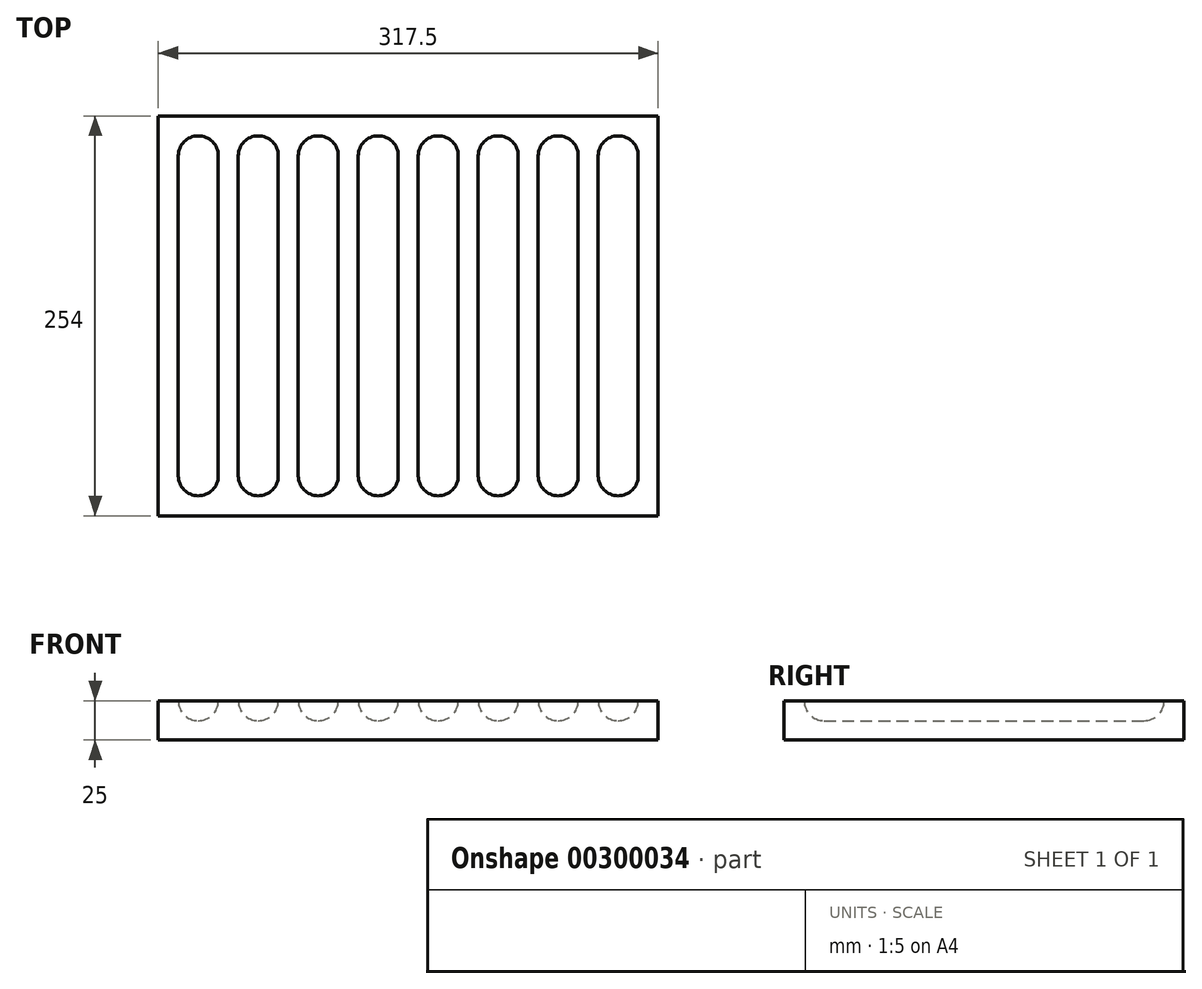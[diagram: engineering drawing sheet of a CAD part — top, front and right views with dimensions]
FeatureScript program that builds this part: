
annotation { "Feature Type Name" : "Feature", "Feature Type Description" : "" }
export const myFeature = defineFeature(function(context is Context, id is Id, definition is map)
    precondition{}
    {
        {
            var Q0;
            Q0=qCreatedBy(makeId("Top.planeOp"),FACE);
            var sketch = newSketch(context, id + "F0", { "sketchPlane" : qUnion([Q0])});
            skLineSegment(sketch, "E0.bottom", {"start": v(-140.22, 133.8) * mm, "end": v(177.28, 133.8) * mm});
            skLineSegment(sketch, "E0.top", {"start": v(-140.22, -120.2) * mm, "end": v(177.28, -120.2) * mm});
            skLineSegment(sketch, "E0.left", {"start": v(-140.22, 133.8) * mm, "end": v(-140.22, -120.2) * mm});
            skLineSegment(sketch, "E0.right", {"start": v(177.28, 133.8) * mm, "end": v(177.28, -120.2) * mm});
            skLineSegment(sketch, "E1.bottom", {"start": v(-127.52, 108.4) * mm, "end": v(-102.12, 108.4) * mm, "construction": true});
            skLineSegment(sketch, "E1.top", {"start": v(-127.52, -94.8) * mm, "end": v(-102.12, -94.8) * mm, "construction": true});
            skLineSegment(sketch, "E1.left", {"start": v(-127.52, 108.4) * mm, "end": v(-127.52, -94.8) * mm});
            skLineSegment(sketch, "E1.right", {"start": v(-102.12, 108.4) * mm, "end": v(-102.12, -94.8) * mm});
            skArc(sketch, "E2", {"start": v(-127.52, 108.4) * mm, "mid": v(-114.82, 121.1) * mm, "end": v(-102.12, 108.4) * mm});
            skArc(sketch, "E3", {"start": v(-102.12, -94.8) * mm, "mid": v(-114.82, -107.5) * mm, "end": v(-127.52, -94.8) * mm});
            skLineSegment(sketch, "E4.1.0.0", {"start": v(-89.42, 108.4) * mm, "end": v(-89.42, -94.8) * mm});
            skArc(sketch, "E4.1.0.1", {"start": v(-89.42, 108.4) * mm, "mid": v(-76.72, 121.1) * mm, "end": v(-64.02, 108.4) * mm});
            skLineSegment(sketch, "E4.1.0.2", {"start": v(-64.02, 108.4) * mm, "end": v(-64.02, -94.8) * mm});
            skArc(sketch, "E4.1.0.3", {"start": v(-64.02, -94.8) * mm, "mid": v(-76.72, -107.5) * mm, "end": v(-89.42, -94.8) * mm});
            skLineSegment(sketch, "E4.1.0.4", {"start": v(-89.42, -94.8) * mm, "end": v(-64.02, -94.8) * mm, "construction": true});
            skLineSegment(sketch, "E4.1.0.5", {"start": v(-89.42, 108.4) * mm, "end": v(-64.02, 108.4) * mm, "construction": true});
            skLineSegment(sketch, "E4.2.0.0", {"start": v(-51.32, 108.4) * mm, "end": v(-51.32, -94.8) * mm});
            skArc(sketch, "E4.2.0.1", {"start": v(-51.32, 108.4) * mm, "mid": v(-38.62, 121.1) * mm, "end": v(-25.92, 108.4) * mm});
            skLineSegment(sketch, "E4.2.0.2", {"start": v(-25.92, 108.4) * mm, "end": v(-25.92, -94.8) * mm});
            skArc(sketch, "E4.2.0.3", {"start": v(-25.92, -94.8) * mm, "mid": v(-38.62, -107.5) * mm, "end": v(-51.32, -94.8) * mm});
            skLineSegment(sketch, "E4.2.0.4", {"start": v(-51.32, -94.8) * mm, "end": v(-25.92, -94.8) * mm, "construction": true});
            skLineSegment(sketch, "E4.2.0.5", {"start": v(-51.32, 108.4) * mm, "end": v(-25.92, 108.4) * mm, "construction": true});
            skLineSegment(sketch, "E4.3.0.0", {"start": v(-13.22, 108.4) * mm, "end": v(-13.22, -94.8) * mm});
            skArc(sketch, "E4.3.0.1", {"start": v(-13.22, 108.4) * mm, "mid": v(-0.52, 121.1) * mm, "end": v(12.18, 108.4) * mm});
            skLineSegment(sketch, "E4.3.0.2", {"start": v(12.18, 108.4) * mm, "end": v(12.18, -94.8) * mm});
            skArc(sketch, "E4.3.0.3", {"start": v(12.18, -94.8) * mm, "mid": v(-0.52, -107.5) * mm, "end": v(-13.22, -94.8) * mm});
            skLineSegment(sketch, "E4.3.0.4", {"start": v(-13.22, -94.8) * mm, "end": v(12.18, -94.8) * mm, "construction": true});
            skLineSegment(sketch, "E4.3.0.5", {"start": v(-13.22, 108.4) * mm, "end": v(12.18, 108.4) * mm, "construction": true});
            skLineSegment(sketch, "E4.4.0.0", {"start": v(24.88, 108.4) * mm, "end": v(24.88, -94.8) * mm});
            skArc(sketch, "E4.4.0.1", {"start": v(24.88, 108.4) * mm, "mid": v(37.58, 121.1) * mm, "end": v(50.28, 108.4) * mm});
            skLineSegment(sketch, "E4.4.0.2", {"start": v(50.28, 108.4) * mm, "end": v(50.28, -94.8) * mm});
            skArc(sketch, "E4.4.0.3", {"start": v(50.28, -94.8) * mm, "mid": v(37.58, -107.5) * mm, "end": v(24.88, -94.8) * mm});
            skLineSegment(sketch, "E4.4.0.4", {"start": v(24.88, -94.8) * mm, "end": v(50.28, -94.8) * mm, "construction": true});
            skLineSegment(sketch, "E4.4.0.5", {"start": v(24.88, 108.4) * mm, "end": v(50.28, 108.4) * mm, "construction": true});
            skLineSegment(sketch, "E4.5.0.0", {"start": v(62.98, 108.4) * mm, "end": v(62.98, -94.8) * mm});
            skArc(sketch, "E4.5.0.1", {"start": v(62.98, 108.4) * mm, "mid": v(75.68, 121.1) * mm, "end": v(88.38, 108.4) * mm});
            skLineSegment(sketch, "E4.5.0.2", {"start": v(88.38, 108.4) * mm, "end": v(88.38, -94.8) * mm});
            skArc(sketch, "E4.5.0.3", {"start": v(88.38, -94.8) * mm, "mid": v(75.68, -107.5) * mm, "end": v(62.98, -94.8) * mm});
            skLineSegment(sketch, "E4.5.0.4", {"start": v(62.98, -94.8) * mm, "end": v(88.38, -94.8) * mm, "construction": true});
            skLineSegment(sketch, "E4.5.0.5", {"start": v(62.98, 108.4) * mm, "end": v(88.38, 108.4) * mm, "construction": true});
            skLineSegment(sketch, "E4.6.0.0", {"start": v(101.08, 108.4) * mm, "end": v(101.08, -94.8) * mm});
            skArc(sketch, "E4.6.0.1", {"start": v(101.08, 108.4) * mm, "mid": v(113.78, 121.1) * mm, "end": v(126.48, 108.4) * mm});
            skLineSegment(sketch, "E4.6.0.2", {"start": v(126.48, 108.4) * mm, "end": v(126.48, -94.8) * mm});
            skArc(sketch, "E4.6.0.3", {"start": v(126.48, -94.8) * mm, "mid": v(113.78, -107.5) * mm, "end": v(101.08, -94.8) * mm});
            skLineSegment(sketch, "E4.6.0.4", {"start": v(101.08, -94.8) * mm, "end": v(126.48, -94.8) * mm, "construction": true});
            skLineSegment(sketch, "E4.6.0.5", {"start": v(101.08, 108.4) * mm, "end": v(126.48, 108.4) * mm, "construction": true});
            skLineSegment(sketch, "E4.7.0.0", {"start": v(139.18, 108.4) * mm, "end": v(139.18, -94.8) * mm});
            skArc(sketch, "E4.7.0.1", {"start": v(139.18, 108.4) * mm, "mid": v(151.88, 121.1) * mm, "end": v(164.58, 108.4) * mm});
            skLineSegment(sketch, "E4.7.0.2", {"start": v(164.58, 108.4) * mm, "end": v(164.58, -94.8) * mm});
            skArc(sketch, "E4.7.0.3", {"start": v(164.58, -94.8) * mm, "mid": v(151.88, -107.5) * mm, "end": v(139.18, -94.8) * mm});
            skLineSegment(sketch, "E4.7.0.4", {"start": v(139.18, -94.8) * mm, "end": v(164.58, -94.8) * mm, "construction": true});
            skLineSegment(sketch, "E4.7.0.5", {"start": v(139.18, 108.4) * mm, "end": v(164.58, 108.4) * mm, "construction": true});
            skLineSegment(sketch, "E4.direction1", {"start": v(-127.52, -94.8) * mm, "end": v(-89.42, -94.8) * mm, "construction": true});
            skSolve(sketch);
        }
        {
            var Q0;
            Q0=makeQuery(id+"F0.imprint","IMPRINT",FACE,{"disambiguationData":[TD([[makeQuery(id+"F0.imprint","IMPRINT",EDGE,{"derivedFrom":sQuery(id+"F0.wireOp",EDGE,"E0.bottom")}),-1.0]])]});
            var Q1;
            Q1=makeQuery(id+"F0.imprint","IMPRINT",FACE,{"disambiguationData":[TD([[makeQuery(id+"F0.imprint","IMPRINT",EDGE,{"derivedFrom":sQuery(id+"F0.wireOp",EDGE,"E1.left")}),1.0]])]});
            var Q2;
            Q2=makeQuery(id+"F0.imprint","IMPRINT",FACE,{"disambiguationData":[TD([[makeQuery(id+"F0.imprint","IMPRINT",EDGE,{"derivedFrom":sQuery(id+"F0.wireOp",EDGE,"E4.1.0.0")}),1.0]])]});
            var Q3;
            Q3=makeQuery(id+"F0.imprint","IMPRINT",FACE,{"disambiguationData":[TD([[makeQuery(id+"F0.imprint","IMPRINT",EDGE,{"derivedFrom":sQuery(id+"F0.wireOp",EDGE,"E4.2.0.0")}),1.0]])]});
            var Q4;
            Q4=makeQuery(id+"F0.imprint","IMPRINT",FACE,{"disambiguationData":[TD([[makeQuery(id+"F0.imprint","IMPRINT",EDGE,{"derivedFrom":sQuery(id+"F0.wireOp",EDGE,"E4.3.0.0")}),1.0]])]});
            var Q5;
            Q5=makeQuery(id+"F0.imprint","IMPRINT",FACE,{"disambiguationData":[TD([[makeQuery(id+"F0.imprint","IMPRINT",EDGE,{"derivedFrom":sQuery(id+"F0.wireOp",EDGE,"E4.4.0.0")}),1.0]])]});
            var Q6;
            Q6=makeQuery(id+"F0.imprint","IMPRINT",FACE,{"disambiguationData":[TD([[makeQuery(id+"F0.imprint","IMPRINT",EDGE,{"derivedFrom":sQuery(id+"F0.wireOp",EDGE,"E4.5.0.0")}),1.0]])]});
            var Q7;
            Q7=makeQuery(id+"F0.imprint","IMPRINT",FACE,{"disambiguationData":[TD([[makeQuery(id+"F0.imprint","IMPRINT",EDGE,{"derivedFrom":sQuery(id+"F0.wireOp",EDGE,"E4.6.0.0")}),1.0]])]});
            var Q8;
            Q8=makeQuery(id+"F0.imprint","IMPRINT",FACE,{"disambiguationData":[TD([[makeQuery(id+"F0.imprint","IMPRINT",EDGE,{"derivedFrom":sQuery(id+"F0.wireOp",EDGE,"E4.7.0.0")}),1.0]])]});
            extrude(context, id + "F1", {"entities" : qUnion([Q0, Q1, Q2, Q3, Q4, Q5, Q6, Q7, Q8]), "oppositeDirection" : true, "depth" : 25 * mm});
        }
        {
            var Q0;
            Q0=makeQuery(id+"F0.imprint","IMPRINT",FACE,{"disambiguationData":[TD([[makeQuery(id+"F0.imprint","IMPRINT",EDGE,{"derivedFrom":sQuery(id+"F0.wireOp",EDGE,"E1.left")}),1.0]])]});
            var Q1;
            Q1=makeQuery(id+"F0.imprint","IMPRINT",FACE,{"disambiguationData":[TD([[makeQuery(id+"F0.imprint","IMPRINT",EDGE,{"derivedFrom":sQuery(id+"F0.wireOp",EDGE,"E4.1.0.0")}),1.0]])]});
            var Q2;
            Q2=makeQuery(id+"F0.imprint","IMPRINT",FACE,{"disambiguationData":[TD([[makeQuery(id+"F0.imprint","IMPRINT",EDGE,{"derivedFrom":sQuery(id+"F0.wireOp",EDGE,"E4.2.0.0")}),1.0]])]});
            var Q3;
            Q3=makeQuery(id+"F0.imprint","IMPRINT",FACE,{"disambiguationData":[TD([[makeQuery(id+"F0.imprint","IMPRINT",EDGE,{"derivedFrom":sQuery(id+"F0.wireOp",EDGE,"E4.3.0.0")}),1.0]])]});
            var Q4;
            Q4=makeQuery(id+"F0.imprint","IMPRINT",FACE,{"disambiguationData":[TD([[makeQuery(id+"F0.imprint","IMPRINT",EDGE,{"derivedFrom":sQuery(id+"F0.wireOp",EDGE,"E4.4.0.0")}),1.0]])]});
            var Q5;
            Q5=makeQuery(id+"F0.imprint","IMPRINT",FACE,{"disambiguationData":[TD([[makeQuery(id+"F0.imprint","IMPRINT",EDGE,{"derivedFrom":sQuery(id+"F0.wireOp",EDGE,"E4.5.0.0")}),1.0]])]});
            var Q6;
            Q6=makeQuery(id+"F0.imprint","IMPRINT",FACE,{"disambiguationData":[TD([[makeQuery(id+"F0.imprint","IMPRINT",EDGE,{"derivedFrom":sQuery(id+"F0.wireOp",EDGE,"E4.6.0.0")}),1.0]])]});
            var Q7;
            Q7=makeQuery(id+"F0.imprint","IMPRINT",FACE,{"disambiguationData":[TD([[makeQuery(id+"F0.imprint","IMPRINT",EDGE,{"derivedFrom":sQuery(id+"F0.wireOp",EDGE,"E4.7.0.0")}),1.0]])]});
            extrude(context, id + "F2", {"entities" : qUnion([Q0, Q1, Q2, Q3, Q4, Q5, Q6, Q7]), "operationType" : NewBodyOperationType.REMOVE, "oppositeDirection" : true, "depth" : 12.7 * mm});
        }
        {
            var Q0;
            Q0=makeQuery(id+"F2.boolean.opBoolean","COPY",EDGE,{"derivedFrom":makeQuery(id+"F2.opExtrude","CAP_EDGE",EDGE,{"disambiguationData":[OSD([sQuery(id+"F0.wireOp",EDGE,"E1.left")])],"isStart":false})});
            var Q1;
            Q1=makeQuery(id+"F2.boolean.opBoolean","COPY",EDGE,{"derivedFrom":makeQuery(id+"F2.opExtrude","CAP_EDGE",EDGE,{"disambiguationData":[OSD([sQuery(id+"F0.wireOp",EDGE,"E4.1.0.0")])],"isStart":false})});
            var Q2;
            Q2=makeQuery(id+"F2.boolean.opBoolean","COPY",EDGE,{"derivedFrom":makeQuery(id+"F2.opExtrude","CAP_EDGE",EDGE,{"disambiguationData":[OSD([sQuery(id+"F0.wireOp",EDGE,"E4.2.0.0")])],"isStart":false})});
            var Q3;
            Q3=makeQuery(id+"F2.boolean.opBoolean","COPY",EDGE,{"derivedFrom":makeQuery(id+"F2.opExtrude","CAP_EDGE",EDGE,{"disambiguationData":[OSD([sQuery(id+"F0.wireOp",EDGE,"E4.3.0.0")])],"isStart":false})});
            var Q4;
            Q4=makeQuery(id+"F2.boolean.opBoolean","COPY",EDGE,{"derivedFrom":makeQuery(id+"F2.opExtrude","CAP_EDGE",EDGE,{"disambiguationData":[OSD([sQuery(id+"F0.wireOp",EDGE,"E4.4.0.0")])],"isStart":false})});
            var Q5;
            Q5=makeQuery(id+"F2.boolean.opBoolean","COPY",EDGE,{"derivedFrom":makeQuery(id+"F2.opExtrude","CAP_EDGE",EDGE,{"disambiguationData":[OSD([sQuery(id+"F0.wireOp",EDGE,"E4.5.0.0")])],"isStart":false})});
            var Q6;
            Q6=makeQuery(id+"F2.boolean.opBoolean","COPY",EDGE,{"derivedFrom":makeQuery(id+"F2.opExtrude","CAP_EDGE",EDGE,{"disambiguationData":[OSD([sQuery(id+"F0.wireOp",EDGE,"E4.6.0.0")])],"isStart":false})});
            var Q7;
            Q7=makeQuery(id+"F2.boolean.opBoolean","COPY",EDGE,{"derivedFrom":makeQuery(id+"F2.opExtrude","CAP_EDGE",EDGE,{"disambiguationData":[OSD([sQuery(id+"F0.wireOp",EDGE,"E4.7.0.0")])],"isStart":false})});
            fillet(context, id + "F3", {"entities" : qUnion([Q0, Q1, Q2, Q3, Q4, Q5, Q6, Q7]), "radius" : 12.7 * mm, "tangentPropagation" : true, "allowEdgeOverflow" : false});
        }
    });
